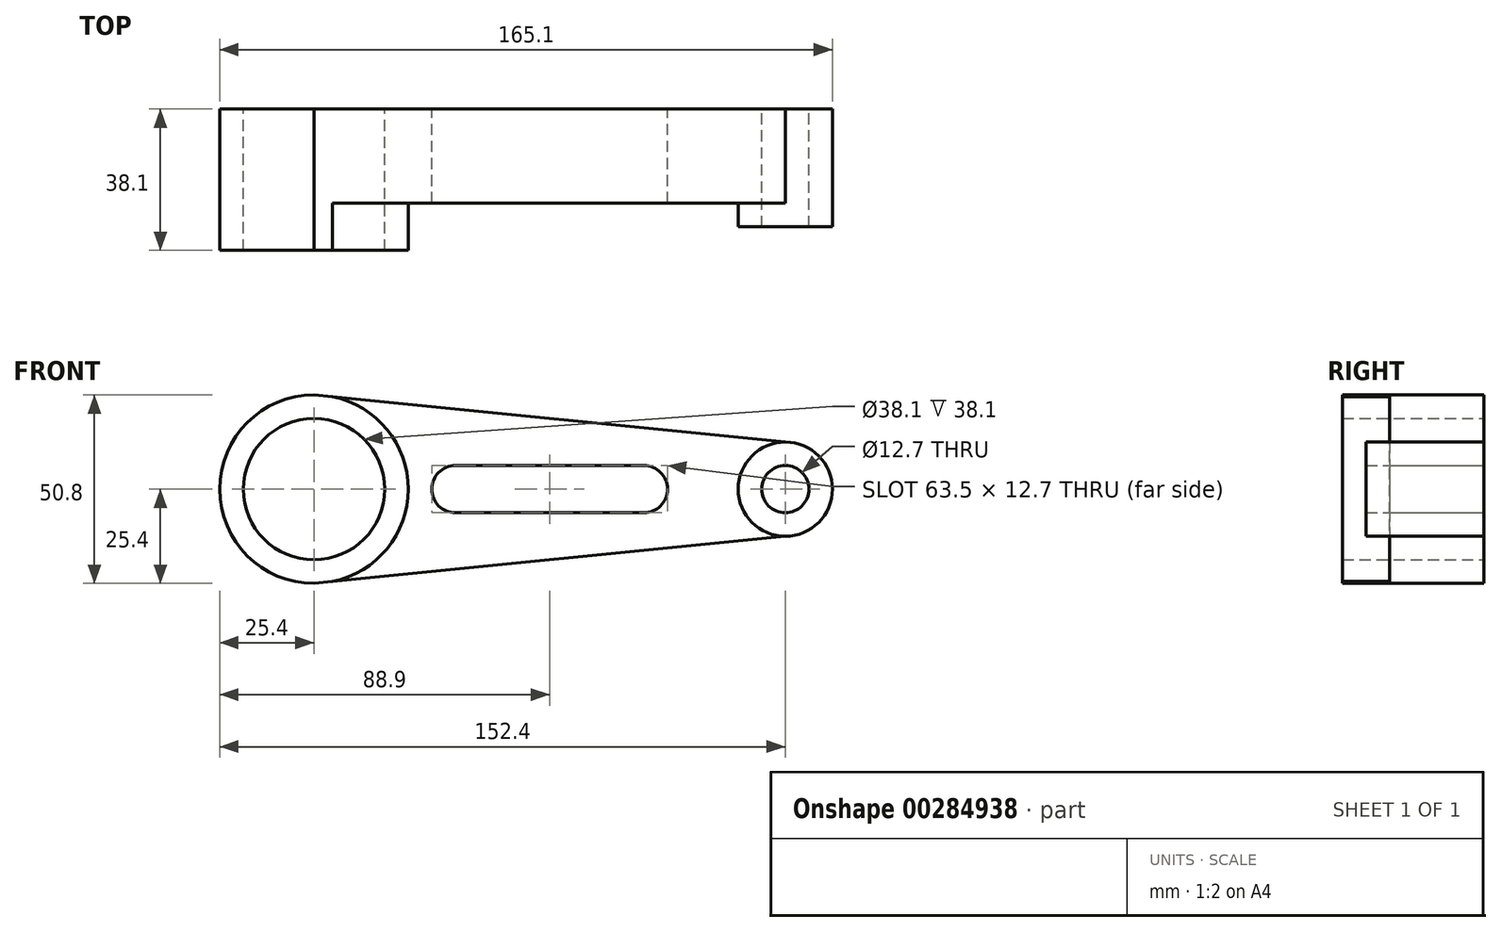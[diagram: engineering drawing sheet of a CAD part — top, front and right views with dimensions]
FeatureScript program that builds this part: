
annotation { "Feature Type Name" : "Feature", "Feature Type Description" : "" }
export const myFeature = defineFeature(function(context is Context, id is Id, definition is map)
    precondition{}
    {
        {
            var Q0;
            Q0=qCreatedBy(makeId("Front.planeOp"),FACE);
            var sketch = newSketch(context, id + "F0", { "sketchPlane" : qUnion([Q0])});
            skCircle(sketch, "E0", {"center": v(0, 0) * mm, "radius": 19.05 * mm});
            skCircle(sketch, "E1", {"center": v(0, 0) * mm, "radius": 25.4 * mm});
            skCircle(sketch, "E2", {"center": v(127, 0) * mm, "radius": 12.7 * mm});
            skCircle(sketch, "E3", {"center": v(127, 0) * mm, "radius": 6.35 * mm});
            skLineSegment(sketch, "E4", {"start": v(0, 25.4) * mm, "end": v(127, 12.7) * mm});
            skLineSegment(sketch, "E5", {"start": v(0, -25.4) * mm, "end": v(127, -12.7) * mm});
            skArc(sketch, "E6", {"start": v(38.1, 6.35) * mm, "mid": v(31.75, 0) * mm, "end": v(38.1, -6.35) * mm});
            skArc(sketch, "E7", {"start": v(88.9, -6.35) * mm, "mid": v(95.25, 0) * mm, "end": v(88.9, 6.35) * mm});
            skLineSegment(sketch, "E8", {"start": v(38.1, 6.35) * mm, "end": v(88.9, 6.35) * mm});
            skPoint(sketch, "E9.end.orphan", {"position": v(88.9, 1.38) * mm});
            skPoint(sketch, "E9.start.orphan", {"position": v(38.1, -6.35) * mm});
            skLineSegment(sketch, "E10", {"start": v(38.1, -6.35) * mm, "end": v(88.9, -6.35) * mm});
            skLineSegment(sketch, "E11", {"start": v(0, 0) * mm, "end": v(127, 0) * mm, "construction": true});
            skSolve(sketch);
        }
        {
            var Q0;
            Q0=makeQuery(id+"F0.imprint","IMPRINT",FACE,{"disambiguationData":[TD([[makeQuery(id+"F0.imprint","IMPRINT",EDGE,{"derivedFrom":sQuery(id+"F0.wireOp",EDGE,"E0")}),-1.0]])]});
            extrude(context, id + "F1", {"entities" : qUnion([Q0]), "depth" : 38.1 * mm});
        }
        {
            var Q0;
            Q0=makeQuery(id+"F0.imprint","IMPRINT",FACE,{"disambiguationData":[TD([[makeQuery(id+"F0.imprint","IMPRINT",EDGE,{"derivedFrom":sQuery(id+"F0.wireOp",EDGE,"E6")}),-1.0]])]});
            extrude(context, id + "F2", {"entities" : qUnion([Q0]), "operationType" : NewBodyOperationType.ADD, "depth" : 25.4 * mm});
        }
        {
            var Q0;
            Q0=makeQuery(id+"F0.imprint","IMPRINT",FACE,{"disambiguationData":[TD([[makeQuery(id+"F0.imprint","IMPRINT",EDGE,{"derivedFrom":sQuery(id+"F0.wireOp",EDGE,"E3")}),-1.0]])]});
            extrude(context, id + "F3", {"entities" : qUnion([Q0]), "operationType" : NewBodyOperationType.ADD, "depth" : 31.75 * mm});
        }
    });
